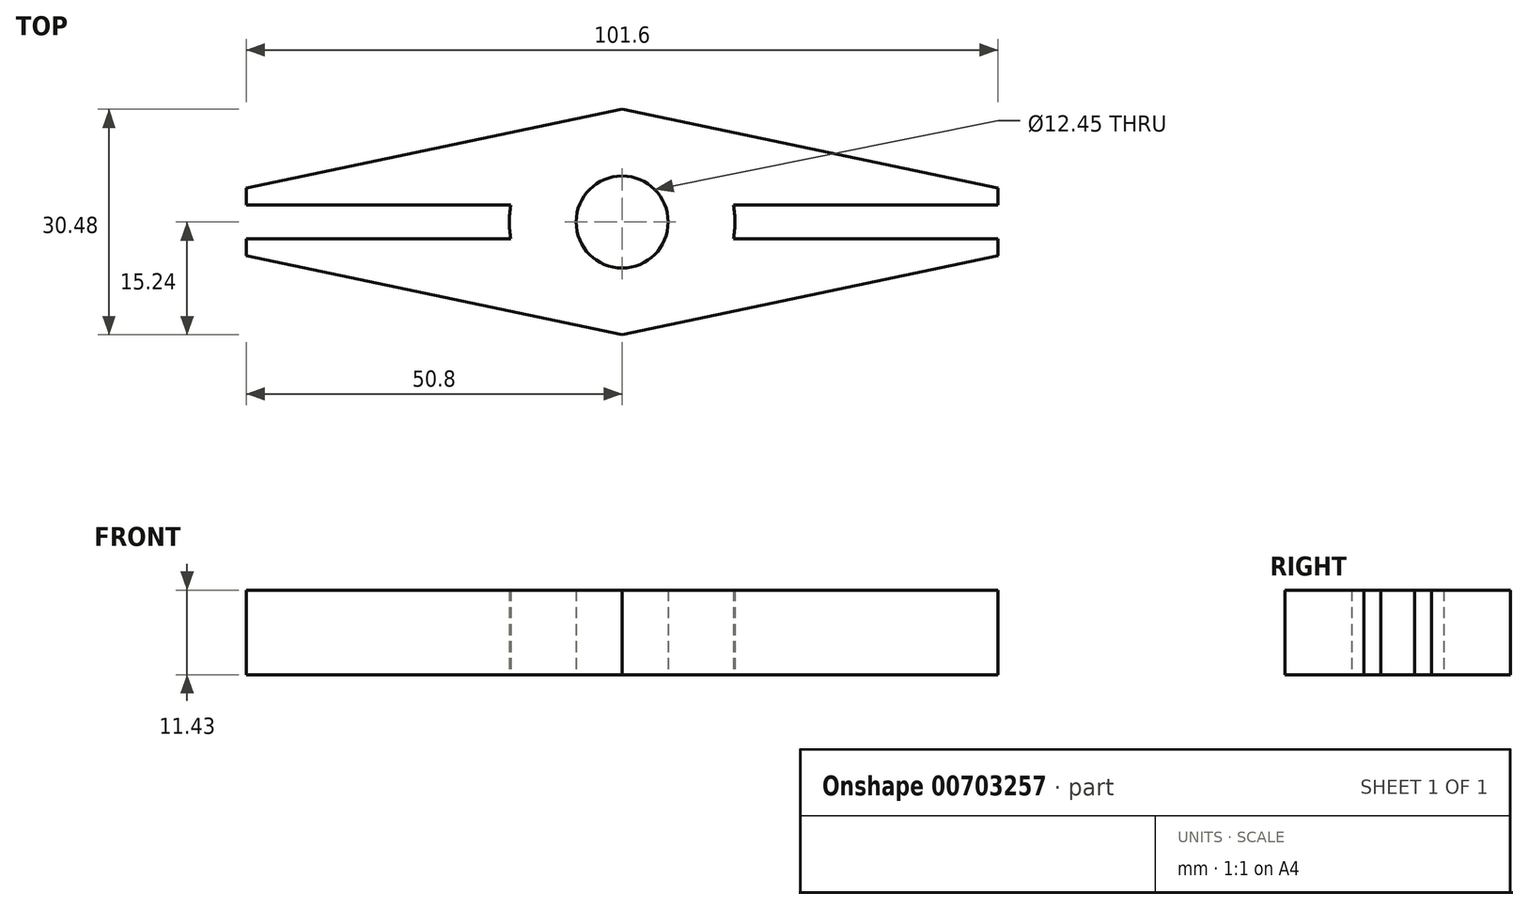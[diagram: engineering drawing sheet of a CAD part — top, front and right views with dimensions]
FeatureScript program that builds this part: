
annotation { "Feature Type Name" : "Feature", "Feature Type Description" : "" }
export const myFeature = defineFeature(function(context is Context, id is Id, definition is map)
    precondition{}
    {
        {
            var Q0;
            Q0=qCreatedBy(makeId("Top.planeOp"),FACE);
            var sketch = newSketch(context, id + "F0", { "sketchPlane" : qUnion([Q0])});
            skCircle(sketch, "E0", {"center": v(0, 0) * mm, "radius": 6.22 * mm});
            skLineSegment(sketch, "E1", {"start": v(0, 0) * mm, "end": v(0, 17.78) * mm, "construction": true});
            skLineSegment(sketch, "E2", {"start": v(0, 0) * mm, "end": v(50.8, 0) * mm, "construction": true});
            skLineSegment(sketch, "E3", {"start": v(0, 0) * mm, "end": v(-50.8, 0) * mm, "construction": true});
            skLineSegment(sketch, "E4", {"start": v(0, 0) * mm, "end": v(0, -17.78) * mm, "construction": true});
            skLineSegment(sketch, "E5", {"start": v(0, 0) * mm, "end": v(-25.4, 0) * mm, "construction": true});
            skLineSegment(sketch, "E6", {"start": v(0, 0) * mm, "end": v(25.4, 0) * mm, "construction": true});
            skCircle(sketch, "E7", {"center": v(0, 0) * mm, "radius": 15.24 * mm});
            skLineSegment(sketch, "E8", {"start": v(-50.8, 0) * mm, "end": v(-50.8, 4.57) * mm, "construction": true});
            skLineSegment(sketch, "E9", {"start": v(-50.8, 0) * mm, "end": v(-50.8, -4.57) * mm, "construction": true});
            skLineSegment(sketch, "E10", {"start": v(-50.8, 4.57) * mm, "end": v(0, 15.24) * mm});
            skLineSegment(sketch, "E11", {"start": v(0, -15.24) * mm, "end": v(50.8, -4.57) * mm});
            skLineSegment(sketch, "E12", {"start": v(0, 15.24) * mm, "end": v(50.8, 4.57) * mm});
            skLineSegment(sketch, "E13", {"start": v(-50.8, -4.57) * mm, "end": v(0, -15.24) * mm});
            skLineSegment(sketch, "E14", {"start": v(-50.8, -4.57) * mm, "end": v(-50.8, -2.29) * mm});
            skLineSegment(sketch, "E15", {"start": v(-50.8, 4.57) * mm, "end": v(-50.8, 2.29) * mm});
            skLineSegment(sketch, "E16", {"start": v(-50.8, -2.29) * mm, "end": v(-15.07, -2.29) * mm});
            skLineSegment(sketch, "E17", {"start": v(-50.8, 2.29) * mm, "end": v(-15.07, 2.29) * mm});
            skLineSegment(sketch, "E18.MirrorCS", {"start": v(50.8, 2.29) * mm, "end": v(15.07, 2.29) * mm});
            skLineSegment(sketch, "E19.MirrorCS", {"start": v(50.8, -2.29) * mm, "end": v(15.07, -2.29) * mm});
            skLineSegment(sketch, "E20", {"start": v(50.8, -4.57) * mm, "end": v(50.8, -2.29) * mm});
            skLineSegment(sketch, "E21", {"start": v(50.8, 4.57) * mm, "end": v(50.8, 2.29) * mm});
            skSolve(sketch);
        }
        {
            var Q0;
            Q0=makeQuery(id+"F0.imprint","IMPRINT",FACE,{"disambiguationData":[TD([[makeQuery(id+"F0.imprint","IMPRINT",EDGE,{"derivedFrom":sQuery(id+"F0.wireOp",EDGE,"E0")}),-1.0]])]});
            var Q1;
            {var subQ0=sQuery(id+"F0.wireOp",EDGE,"E18.MirrorCS");Q1=makeQuery(id+"F0.imprint","IMPRINT",FACE,{"disambiguationData":[TD([[makeQuery(id+"F0.imprint","IMPRINT",EDGE,{"derivedFrom":subQ0}),-1.0]])]});}
            var Q2;
            {var subQ0=sQuery(id+"F0.wireOp",EDGE,"E19.MirrorCS");Q2=makeQuery(id+"F0.imprint","IMPRINT",FACE,{"disambiguationData":[TD([[makeQuery(id+"F0.imprint","IMPRINT",EDGE,{"derivedFrom":subQ0}),1.0]])]});}
            var Q3;
            {var subQ4=sQuery(id+"F0.wireOp",EDGE,"E14");Q3=makeQuery(id+"F0.imprint","IMPRINT",FACE,{"disambiguationData":[TD([[makeQuery(id+"F0.imprint","IMPRINT",EDGE,{"derivedFrom":subQ4}),-1.0]])]});}
            var Q4;
            {var subQ4=sQuery(id+"F0.wireOp",EDGE,"E15");Q4=makeQuery(id+"F0.imprint","IMPRINT",FACE,{"disambiguationData":[TD([[makeQuery(id+"F0.imprint","IMPRINT",EDGE,{"derivedFrom":subQ4}),1.0]])]});}
            extrude(context, id + "F1", {"entities" : qUnion([Q0, Q1, Q2, Q3, Q4]), "depth" : 11.43 * mm, "offsetDistance" : 25.4 * mm});
        }
    });
